# Revit family: Sink-Undercounter-American_Standard-Orbit-0630.000.020.rfaxxx
name_source: partatom
category: Plumbing Fixtures
units: mm (PartAtom-declared; Revit-internal decimal feet)

## family parameters
Always vertical = Yes
Cut with Voids When Loaded = Yes
OmniClass Number = 23.45.05.14.14
OmniClass Title = Sinks/Lavatories
Part Type = Normal
Room Calculation Point = No
Round Connector Dimension = Use Diameter
Shared = Yes
Work Plane-Based = Yes

## types (1)
- 0630.000.020
    4" Centerset = Yes
    8" Spread = No
    ADA Compliant = Yes
    ASME A112.19.2M for Vitreous China Fixtures = Yes
    Assembly Code = D2010310
    Basin Shape = Round
    CAN/CSA B45 series = Yes
    CW Connection = Yes
    CWFU = 1.5
    Cold Water Connection Diameter = 1/2"
    Default Elevation = 0"
    Description = Orbit® Under Counter Sink
    Diameter = 15 1/2"
    Faucet Hole Diameter = 1 1/16"
    Faucet Hole Setback (min. 2") = 2"
    Faucet Hole Setback Constraint = 2"
    Finish = Vitreous China-American Standard-020-White
    Fitting Width = 4"
    HW Connection = Yes
    HWFU = 1.5
    Height = 6"
    Hot Water Connection Diameter = 1"
    Installation Type = Undercounter
    Manufacturer = American Standard
    Material = Vitreous China-American Standard-020-White
    Model = 0630.000.020
    Price = Prices may vary. Please consult Manufacturer Representative for most up-to-date price list.
    Product Documentation Link = https://americanstandard.box.com
    Product Page URL = https://www.americanstandard-us.com
    Revised Date = 03/18/2023
    URL = http://www.americanstandard-us.com
    Vent Connection = No
    WFU = 2
    Waste Connection = Yes
    Waste Connection Diameter = 1 1/4"

## geometry (parser evidence)
native form markers: Sweep x2
no freeform markers — native parametric forms only
